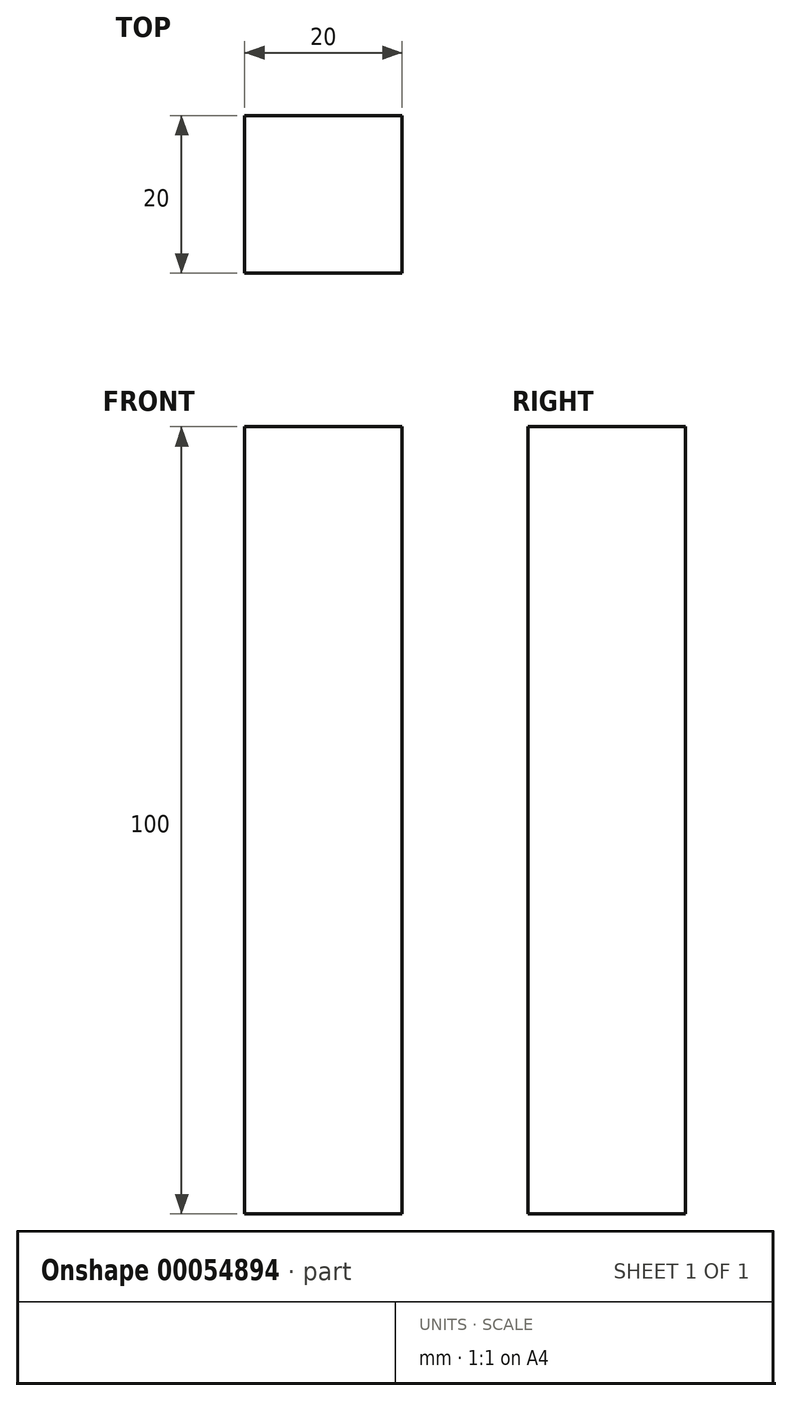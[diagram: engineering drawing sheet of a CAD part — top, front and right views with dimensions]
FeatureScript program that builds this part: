
annotation { "Feature Type Name" : "Feature", "Feature Type Description" : "" }
export const myFeature = defineFeature(function(context is Context, id is Id, definition is map)
    precondition{}
    {
        {
            var Q0;
            Q0=qCreatedBy(makeId("Top.planeOp"),FACE);
            var sketch = newSketch(context, id + "F0", { "sketchPlane" : qUnion([Q0])});
            skLineSegment(sketch, "E0.bottom", {"start": v(-10, 10) * mm, "end": v(10, 10) * mm});
            skLineSegment(sketch, "E0.top", {"start": v(-10, -10) * mm, "end": v(10, -10) * mm});
            skLineSegment(sketch, "E0.left", {"start": v(-10, 10) * mm, "end": v(-10, -10) * mm});
            skLineSegment(sketch, "E0.right", {"start": v(10, 10) * mm, "end": v(10, -10) * mm});
            skPoint(sketch, "E0.middle", {"position": v(0, 0) * mm});
            skSolve(sketch);
        }
        {
            var Q0;
            Q0 = qSketchRegion(id + "F0", true);
            extrude(context, id + "F1", {"entities" : qUnion([Q0]), "depth" : 100 * mm});
        }
    });
